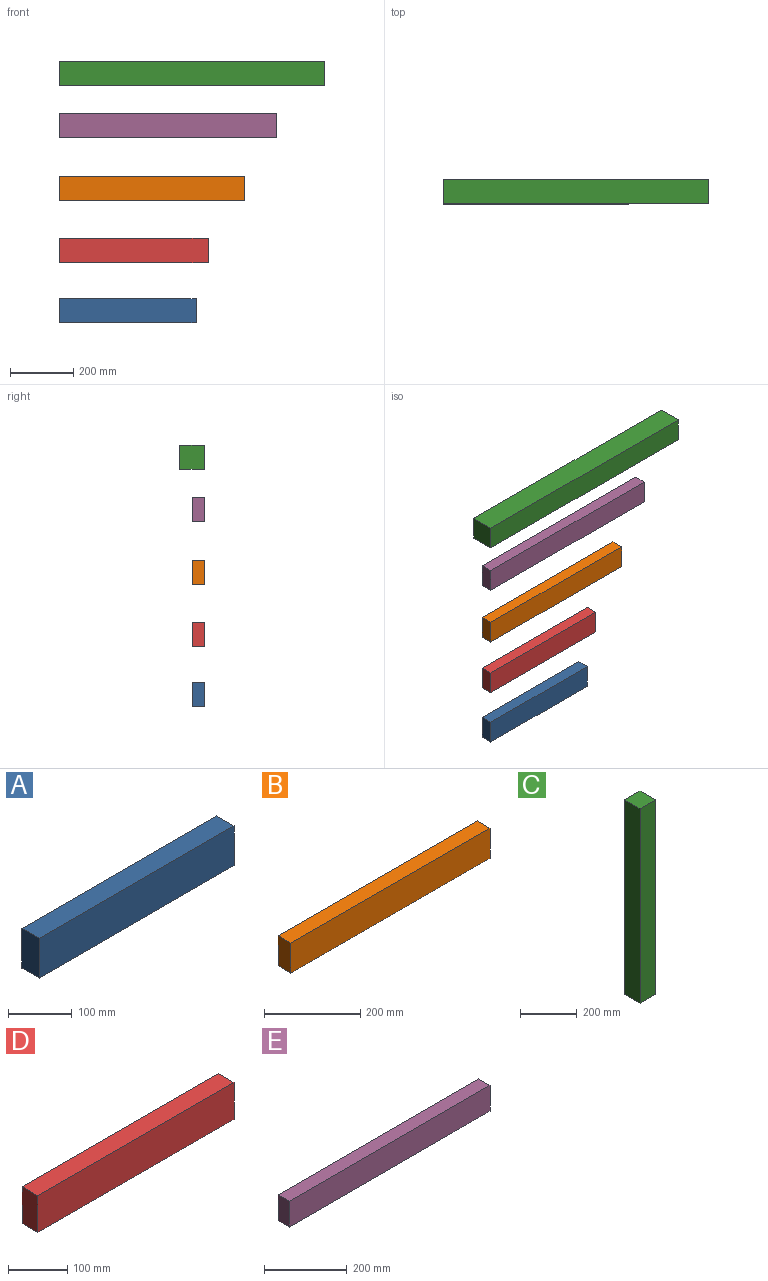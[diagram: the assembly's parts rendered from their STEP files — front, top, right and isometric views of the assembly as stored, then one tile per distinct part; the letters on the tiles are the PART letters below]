
ASSEMBLY  parts=5 mates=4
PART A: 6 faces, bbox 431.8x38.1x76.2 mm
  f0: plane 76.2x38.1mm, normal (-1,0,0), area 2903.2mm2, adj f1,f3,f4,f5
  f1: plane 431.8x38.1mm, normal (0,0,-1), area 16451.6mm2, adj f0,f2,f4,f5
  f2: plane 76.2x38.1mm, normal (1,0,0), area 2903.2mm2, adj f1,f3,f4,f5
  f3: plane 431.8x38.1mm, normal (0,0,1), area 16451.6mm2, adj f0,f2,f4,f5
  f4: plane 431.8x76.2mm, normal (0,-1,0), area 32903.2mm2, adj f0,f1,f2,f3
  f5: plane 431.8x76.2mm, normal (0,1,0), area 32903.2mm2, adj f0,f1,f2,f3
PART B: 6 faces, bbox 584.2x38.1x76.2 mm
  f0: plane 76.2x38.1mm, normal (-1,0,0), area 2903.2mm2, adj f1,f3,f4,f5
  f1: plane 584.2x38.1mm, normal (0,0,-1), area 22258mm2, adj f0,f2,f4,f5
  f2: plane 76.2x38.1mm, normal (1,0,0), area 2903.2mm2, adj f1,f3,f4,f5
  f3: plane 584.2x38.1mm, normal (0,0,1), area 22258mm2, adj f0,f2,f4,f5
  f4: plane 584.2x76.2mm, normal (0,-1,0), area 44516mm2, adj f0,f1,f2,f3
  f5: plane 584.2x76.2mm, normal (0,1,0), area 44516mm2, adj f0,f1,f2,f3
PART C: 6 faces, bbox 76.2x76.2x838.2 mm
  f0: plane 838.2x76.2mm, normal (-1,0,0), area 63870.8mm2, adj f1,f3,f4,f5
  f1: plane 76.2x76.2mm, normal (0,0,-1), area 5806.4mm2, adj f0,f2,f4,f5
  f2: plane 838.2x76.2mm, normal (1,0,0), area 63870.8mm2, adj f1,f3,f4,f5
  f3: plane 76.2x76.2mm, normal (0,0,1), area 5806.4mm2, adj f0,f2,f4,f5
  f4: plane 838.2x76.2mm, normal (0,-1,0), area 63870.8mm2, adj f0,f1,f2,f3
  f5: plane 838.2x76.2mm, normal (0,1,0), area 63870.8mm2, adj f0,f1,f2,f3
PART D: 6 faces, bbox 469.9x38.1x76.2 mm
  f0: plane 76.2x38.1mm, normal (-1,0,0), area 2903.2mm2, adj f1,f3,f4,f5
  f1: plane 469.9x38.1mm, normal (0,0,-1), area 17903.2mm2, adj f0,f2,f4,f5
  f2: plane 76.2x38.1mm, normal (1,0,0), area 2903.2mm2, adj f1,f3,f4,f5
  f3: plane 469.9x38.1mm, normal (0,0,1), area 17903.2mm2, adj f0,f2,f4,f5
  f4: plane 469.9x76.2mm, normal (0,-1,0), area 35806.4mm2, adj f0,f1,f2,f3
  f5: plane 469.9x76.2mm, normal (0,1,0), area 35806.4mm2, adj f0,f1,f2,f3
PART E: 6 faces, bbox 685.8x38.1x76.2 mm
  f0: plane 76.2x38.1mm, normal (-1,0,0), area 2903.2mm2, adj f1,f3,f4,f5
  f1: plane 685.8x38.1mm, normal (0,0,-1), area 26129mm2, adj f0,f2,f4,f5
  f2: plane 76.2x38.1mm, normal (1,0,0), area 2903.2mm2, adj f1,f3,f4,f5
  f3: plane 685.8x38.1mm, normal (0,0,1), area 26129mm2, adj f0,f2,f4,f5
  f4: plane 685.8x76.2mm, normal (0,-1,0), area 52258mm2, adj f0,f1,f2,f3
  f5: plane 685.8x76.2mm, normal (0,1,0), area 52258mm2, adj f0,f1,f2,f3
PLACE A t=(-30.32,129.42,76.51)mm
PLACE B t=(-33.73,129.42,265.31)mm
PLACE C rot(axis=(0,1,0),90deg) t=(442.37,167.52,787.67)mm
PLACE D t=(-31.17,129.42,357.57)mm
PLACE E t=(-34.06,129.42,563.78)mm
MATE slider D.f3 <-> A.f1  axis (0,0,1) through (-97.71,91.32,227.75)mm
MATE slider E.f3 <-> C.f2  axis (0,0,1) through (-97.71,91.32,623.51)mm
MATE slider B.f1 <-> A.f3  axis (0,0,-1) through (-97.71,91.32,347.31)mm
MATE slider B.f3 <-> E.f1  axis (0,0,1) through (-97.71,91.32,423.51)mm
